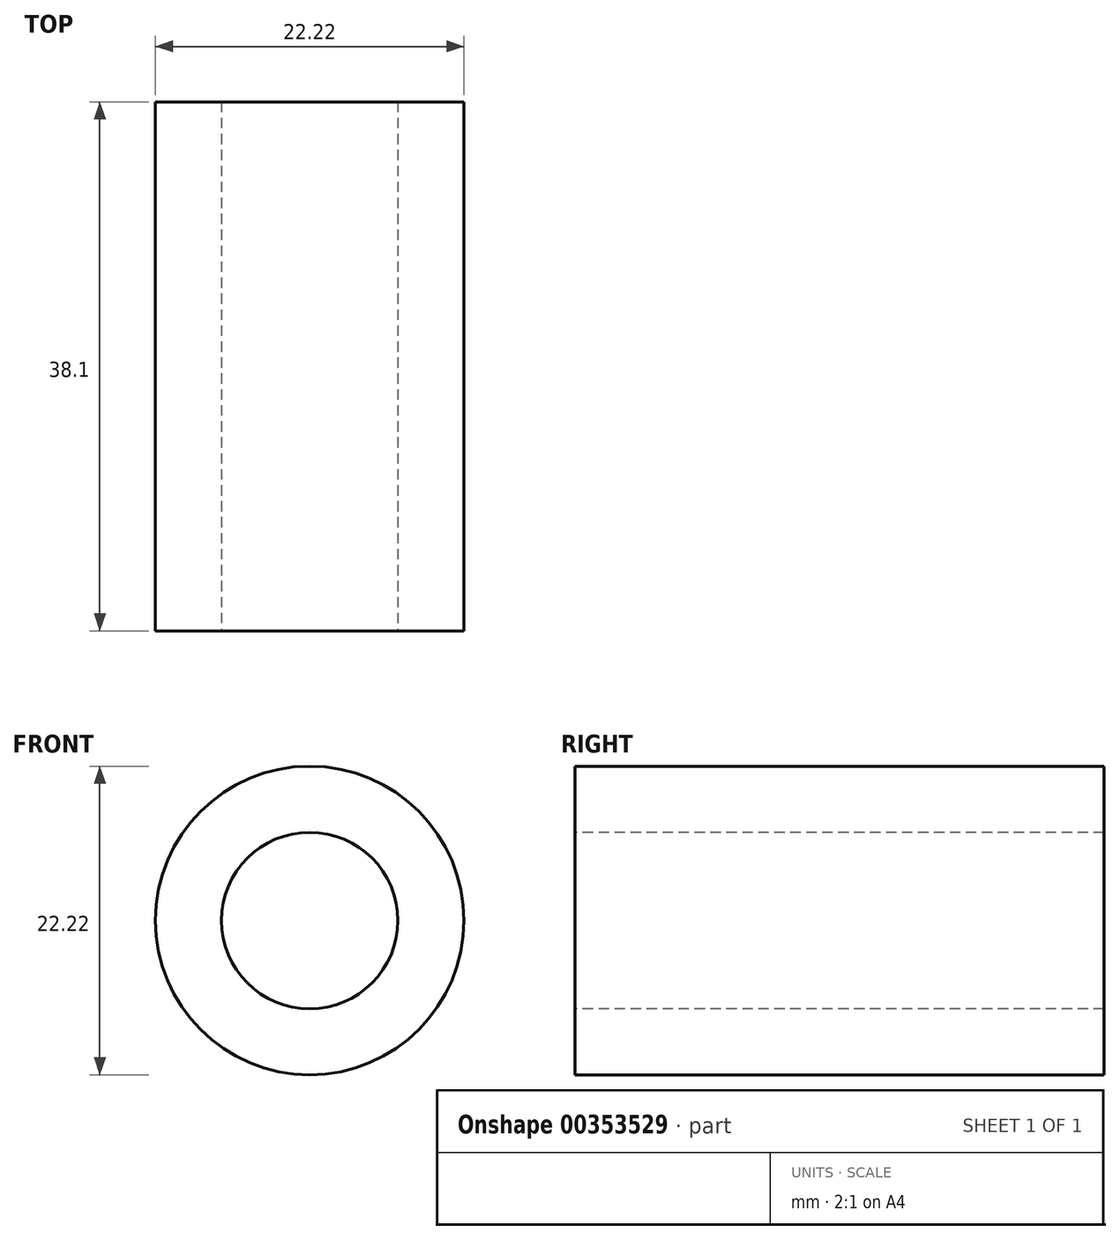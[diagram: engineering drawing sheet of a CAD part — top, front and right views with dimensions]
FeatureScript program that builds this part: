
annotation { "Feature Type Name" : "Feature", "Feature Type Description" : "" }
export const myFeature = defineFeature(function(context is Context, id is Id, definition is map)
    precondition{}
    {
        {
            var Q0;
            Q0=qCreatedBy(makeId("Front.planeOp"),FACE);
            var sketch = newSketch(context, id + "F0", { "sketchPlane" : qUnion([Q0])});
            skCircle(sketch, "E0", {"center": v(0, 0) * mm, "radius": 11.11 * mm});
            skSolve(sketch);
        }
        {
            var Q0;
            Q0=qSketchRegion(id+"F0",true);
            extrude(context, id + "F1", {"entities" : qUnion([Q0]), "depth" : 38.1 * mm, "symmetric" : true});
        }
        {
            var Q0;
            Q0=makeQuery(id+"F1.opExtrude","CAP_FACE",FACE,{"disambiguationData":[OSD([sQuery(id+"F0.wireOp",EDGE,"E0")])],"isStart":false});
            var sketch = newSketch(context, id + "F2", { "sketchPlane" : qUnion([Q0])});
            skCircle(sketch, "E1", {"center": v(0, 0) * mm, "radius": 6.35 * mm});
            skSolve(sketch);
        }
        {
            var Q0;
            Q0=qSketchRegion(id+"F2",true);
            var Q1;
            Q1=makeQuery(id+"F1.opExtrude","CAP_FACE",FACE,{"disambiguationData":[OSD([sQuery(id+"F0.wireOp",EDGE,"E0")])],"isStart":true});
            extrude(context, id + "F3", {"entities" : qUnion([Q0]), "operationType" : NewBodyOperationType.REMOVE, "endBound" : BoundingType.UP_TO_SURFACE, "oppositeDirection" : true, "endBoundEntityFace" : qUnion([Q1]), "depth" : 25.4 * mm});
        }
    });
